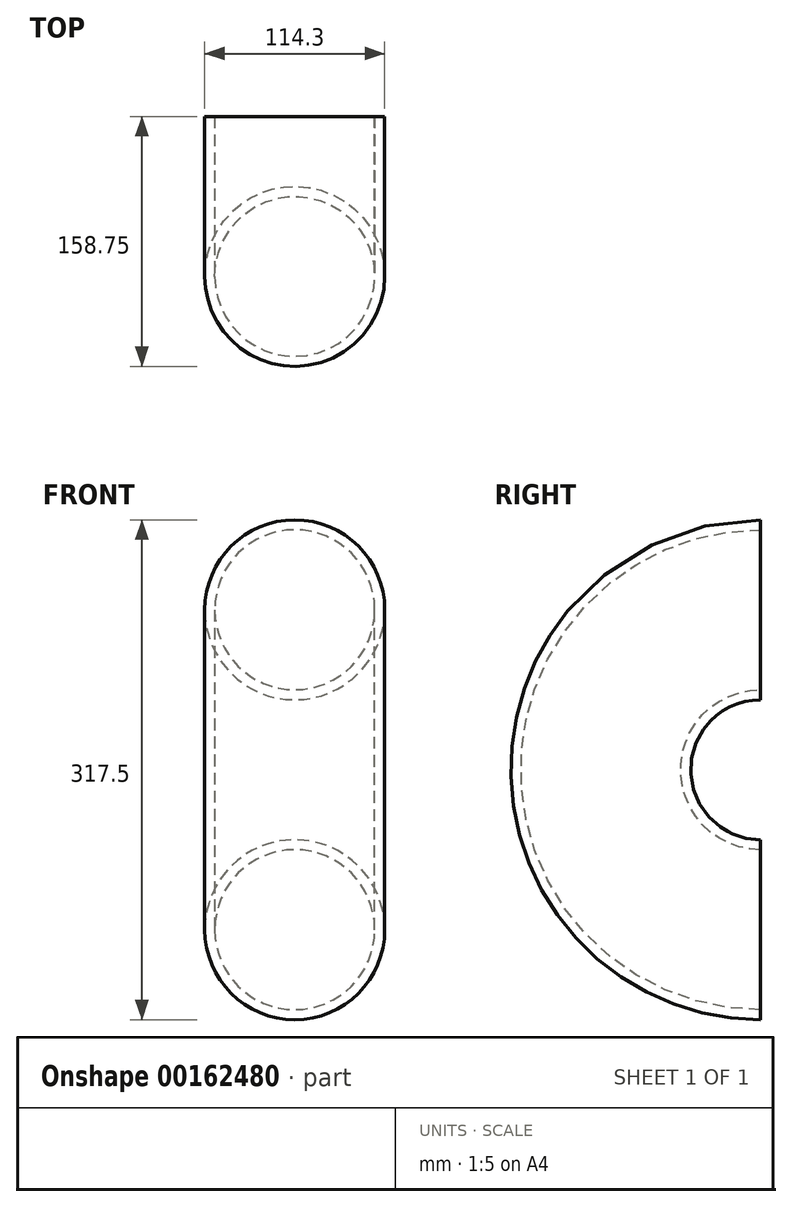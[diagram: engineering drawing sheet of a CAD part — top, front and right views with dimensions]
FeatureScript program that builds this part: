
annotation { "Feature Type Name" : "Feature", "Feature Type Description" : "" }
export const myFeature = defineFeature(function(context is Context, id is Id, definition is map)
    precondition{}
    {
        {
            var Q0;
            Q0=qCreatedBy(makeId("Top.planeOp"),FACE);
            var sketch = newSketch(context, id + "F0", { "sketchPlane" : qUnion([Q0])});
            skCircle(sketch, "E0", {"center": v(0, -101.6) * mm, "radius": 50.8 * mm});
            skCircle(sketch, "E1", {"center": v(0, -101.6) * mm, "radius": 57.15 * mm});
            skLineSegment(sketch, "E2", {"start": v(0, 0) * mm, "end": v(136.3, 0) * mm, "construction": true});
            skSolve(sketch);
        }
        {
            var Q0;
            Q0 = qSketchRegion(id + "F0", true);
            var Q1;
            Q1=sQuery(id+"F0.wireOp",EDGE,"E2");
            revolve(context, id + "F1", {"entities" : qUnion([Q0]), "axis" : qUnion([Q1]), "revolveType" : RevolveType.SYMMETRIC, "angle" : 180 * degree});
        }
    });
